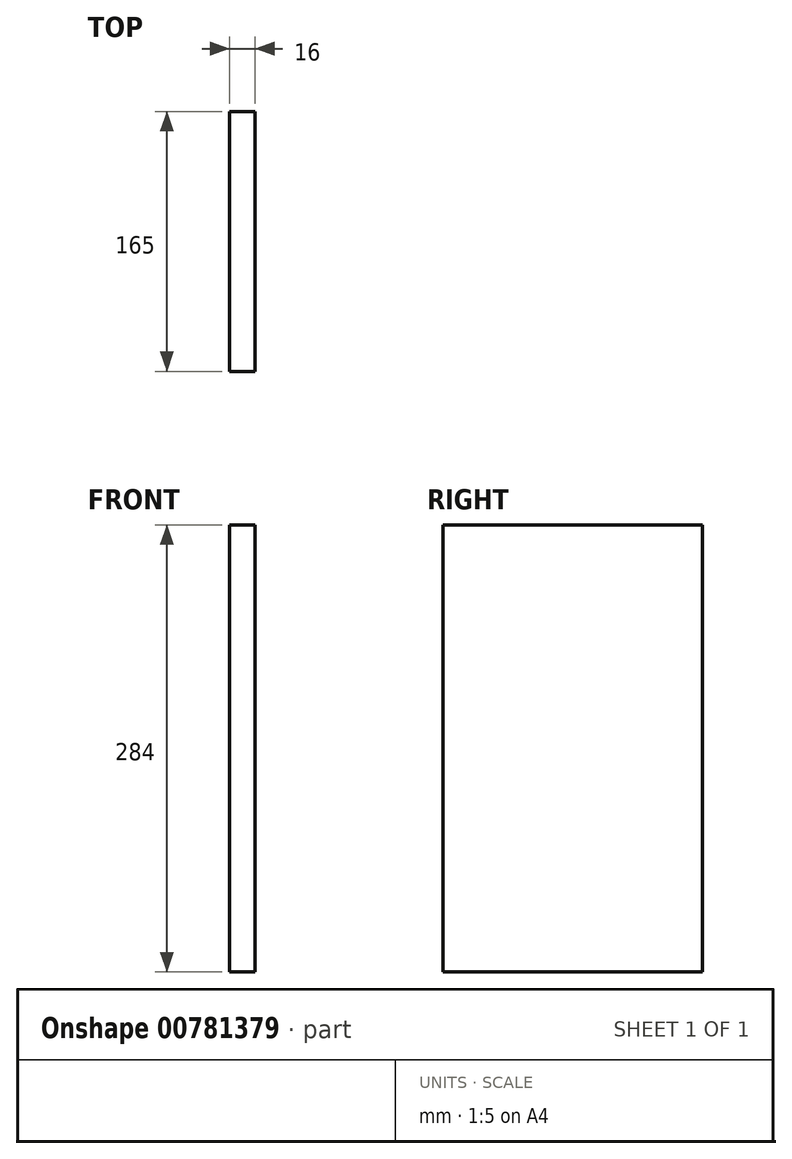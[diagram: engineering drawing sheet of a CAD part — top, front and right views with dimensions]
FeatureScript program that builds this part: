
annotation { "Feature Type Name" : "Feature", "Feature Type Description" : "" }
export const myFeature = defineFeature(function(context is Context, id is Id, definition is map)
    precondition{}
    {
        {
            var Q0;
            Q0=qCreatedBy(makeId("Right.planeOp"),FACE);
            var sketch = newSketch(context, id + "F0", { "sketchPlane" : qUnion([Q0])});
            skLineSegment(sketch, "E0.bottom", {"start": v(82.5, -142) * mm, "end": v(-82.5, -142) * mm});
            skLineSegment(sketch, "E0.top", {"start": v(82.5, 142) * mm, "end": v(-82.5, 142) * mm});
            skLineSegment(sketch, "E0.left", {"start": v(82.5, -142) * mm, "end": v(82.5, 142) * mm});
            skLineSegment(sketch, "E0.right", {"start": v(-82.5, -142) * mm, "end": v(-82.5, 142) * mm});
            skPoint(sketch, "E0.middle", {"position": v(0, 0) * mm});
            skSolve(sketch);
        }
        {
            var Q0;
            Q0=makeQuery(id+"F0.imprint","IMPRINT",FACE,{"disambiguationData":[TD([[makeQuery(id+"F0.imprint","IMPRINT",EDGE,{"derivedFrom":sQuery(id+"F0.wireOp",EDGE,"E0.bottom")}),-1.0]])]});
            extrude(context, id + "F1", {"entities" : qUnion([Q0]), "depth" : 16 * mm, "offsetDistance" : 25 * mm});
        }
    });
